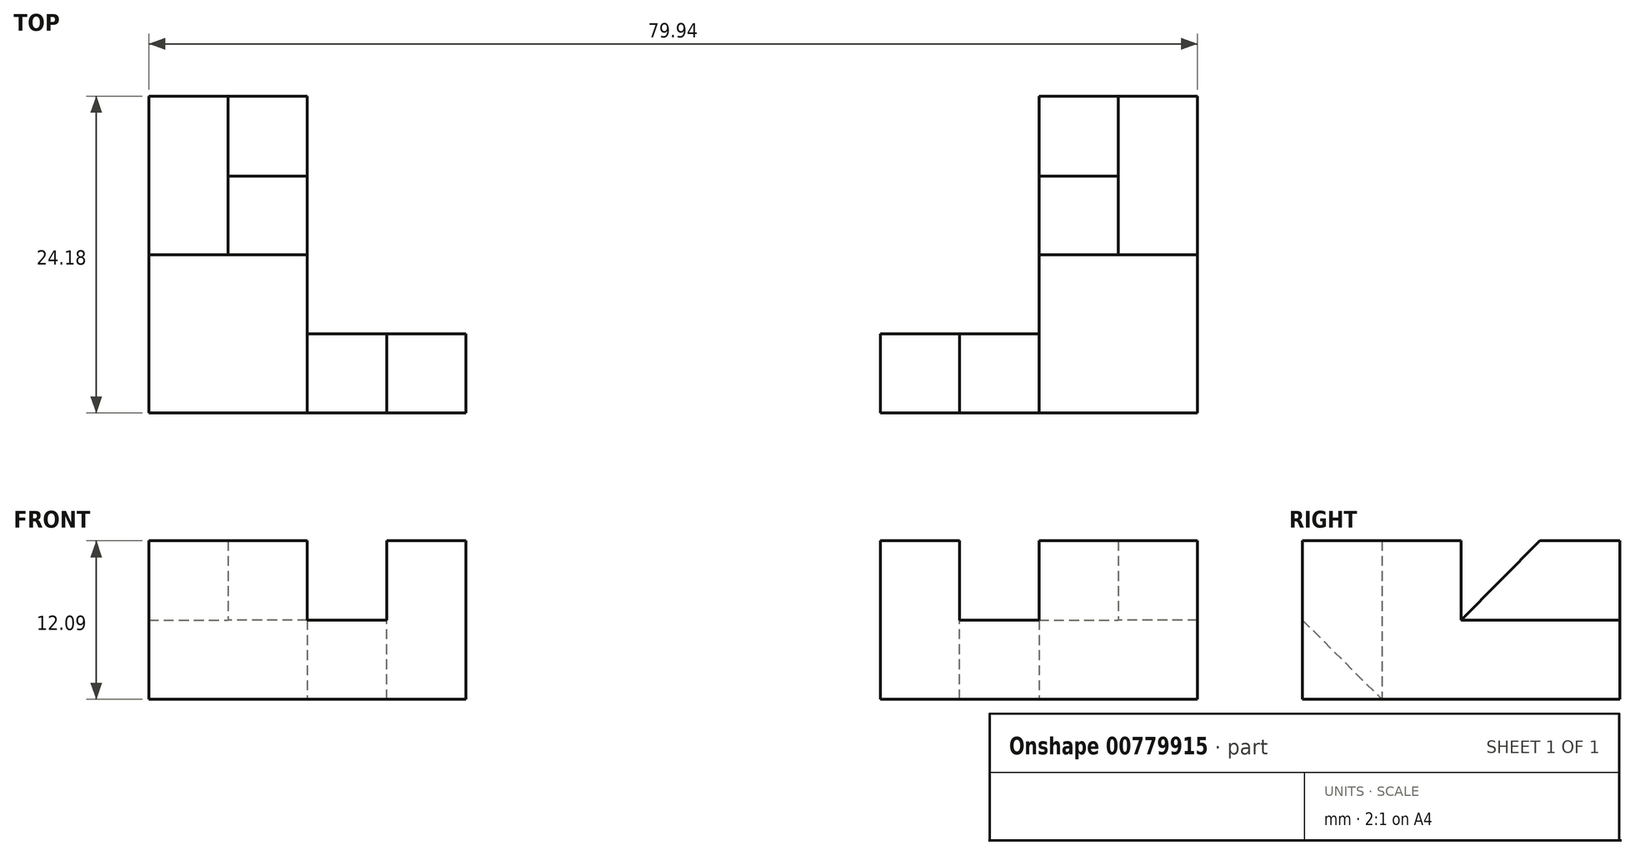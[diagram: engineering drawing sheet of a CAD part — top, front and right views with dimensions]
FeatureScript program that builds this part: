
annotation { "Feature Type Name" : "Feature", "Feature Type Description" : "" }
export const myFeature = defineFeature(function(context is Context, id is Id, definition is map)
    precondition{}
    {
        {
            var Q0;
            Q0=qCreatedBy(makeId("Top.planeOp"),FACE);
            var sketch = newSketch(context, id + "F0", { "sketchPlane" : qUnion([Q0])});
            skLineSegment(sketch, "E0", {"start": v(-15.79, 0) * mm, "end": v(-39.97, 0) * mm});
            skLineSegment(sketch, "E1.bottom", {"start": v(-39.97, 0) * mm, "end": v(-27.88, 0) * mm});
            skLineSegment(sketch, "E1.top", {"start": v(-39.97, 12.1) * mm, "end": v(-27.88, 12.1) * mm});
            skLineSegment(sketch, "E1.left", {"start": v(-39.97, 0) * mm, "end": v(-39.97, 12.1) * mm});
            skLineSegment(sketch, "E1.right", {"start": v(-27.88, 0) * mm, "end": v(-27.88, 12.1) * mm});
            skLineSegment(sketch, "E2", {"start": v(-39.97, 24.18) * mm, "end": v(-33.92, 24.18) * mm});
            skLineSegment(sketch, "E3.bottom", {"start": v(-33.92, 24.18) * mm, "end": v(-27.88, 24.18) * mm});
            skLineSegment(sketch, "E3.top", {"start": v(-33.92, 18.14) * mm, "end": v(-27.88, 18.14) * mm});
            skLineSegment(sketch, "E3.left", {"start": v(-33.92, 24.18) * mm, "end": v(-33.92, 18.14) * mm});
            skLineSegment(sketch, "E3.right", {"start": v(-27.88, 24.18) * mm, "end": v(-27.88, 18.14) * mm});
            skLineSegment(sketch, "E4.top", {"start": v(-33.92, 12.1) * mm, "end": v(-27.88, 12.1) * mm});
            skLineSegment(sketch, "E4.left", {"start": v(-33.92, 18.14) * mm, "end": v(-33.92, 12.1) * mm});
            skLineSegment(sketch, "E4.right", {"start": v(-27.88, 18.14) * mm, "end": v(-27.88, 12.1) * mm});
            skLineSegment(sketch, "E5.bottom", {"start": v(-15.79, 0) * mm, "end": v(-21.83, 0) * mm});
            skLineSegment(sketch, "E5.top", {"start": v(-15.79, 6.05) * mm, "end": v(-21.83, 6.05) * mm});
            skLineSegment(sketch, "E5.left", {"start": v(-15.79, 0) * mm, "end": v(-15.79, 6.05) * mm});
            skLineSegment(sketch, "E5.right", {"start": v(-21.83, 0) * mm, "end": v(-21.83, 6.05) * mm});
            skLineSegment(sketch, "E6.bottom", {"start": v(-21.83, 6.05) * mm, "end": v(-27.88, 6.05) * mm});
            skLineSegment(sketch, "E6.top", {"start": v(-21.83, 0) * mm, "end": v(-27.88, 0) * mm});
            skLineSegment(sketch, "E6.left", {"start": v(-21.83, 6.05) * mm, "end": v(-21.83, 0) * mm});
            skLineSegment(sketch, "E6.right", {"start": v(-27.88, 6.05) * mm, "end": v(-27.88, 0) * mm});
            skLineSegment(sketch, "E7", {"start": v(-39.97, 24.18) * mm, "end": v(-39.97, 12.1) * mm});
            skSolve(sketch);
        }
        {
            var Q0;
            {var subQ4=sQuery(id+"F0.wireOp",EDGE,"E1.left");Q0=makeQuery(id+"F0.imprint","IMPRINT",FACE,{"disambiguationData":[TD([[makeQuery(id+"F0.imprint","IMPRINT",EDGE,{"derivedFrom":subQ4}),-1.0]])]});}
            extrude(context, id + "F1", {"entities" : qUnion([Q0]), "depth" : 12.1 * mm, "offsetDistance" : 25.4 * mm});
        }
        {
            var Q0;
            Q0=makeQuery(id+"F0.imprint","IMPRINT",FACE,{"disambiguationData":[TD([[makeQuery(id+"F0.imprint","IMPRINT",EDGE,{"derivedFrom":sQuery(id+"F0.wireOp",EDGE,"E2")}),-1.0]])]});
            extrude(context, id + "F2", {"entities" : qUnion([Q0]), "operationType" : NewBodyOperationType.ADD, "depth" : 6.05 * mm, "offsetDistance" : 25.4 * mm});
        }
        {
            var Q0;
            Q0=makeQuery(id+"F0.imprint","IMPRINT",FACE,{"disambiguationData":[TD([[makeQuery(id+"F0.imprint","IMPRINT",EDGE,{"derivedFrom":sQuery(id+"F0.wireOp",EDGE,"E3.bottom")}),-1.0]])]});
            extrude(context, id + "F3", {"entities" : qUnion([Q0]), "operationType" : NewBodyOperationType.ADD, "depth" : 12.1 * mm, "offsetDistance" : 25.4 * mm});
        }
        {
            var Q0;
            Q0=makeQuery(id+"F0.imprint","IMPRINT",FACE,{"disambiguationData":[TD([[makeQuery(id+"F0.imprint","IMPRINT",EDGE,{"derivedFrom":sQuery(id+"F0.wireOp",EDGE,"E5.top")}),1.0]])]});
            extrude(context, id + "F4", {"entities" : qUnion([Q0]), "operationType" : NewBodyOperationType.ADD, "depth" : 12.1 * mm, "offsetDistance" : 25.4 * mm});
        }
        {
            var Q0;
            {var subQ3=sQuery(id+"F0.wireOp",EDGE,"E5.right");Q0=makeQuery(id+"F0.imprint","IMPRINT",FACE,{"disambiguationData":[TD([[makeQuery(id+"F0.imprint","IMPRINT",EDGE,{"derivedFrom":subQ3}),1.0]])]});}
            extrude(context, id + "F5", {"entities" : qUnion([Q0]), "operationType" : NewBodyOperationType.ADD, "depth" : 6.05 * mm, "offsetDistance" : 25.4 * mm});
        }
        {
            var Q0;
            Q0=makeQuery(id+"F5.opExtrude","CAP_EDGE",EDGE,{"disambiguationData":[OSD([sQuery(id+"F0.wireOp",EDGE,"E6.bottom")])],"isStart":false});
            chamfer(context, id + "F6", {"entities" : qUnion([Q0]), "width" : 6.05 * mm, "tangentPropagation" : true});
        }
        {
            var Q0;
            Q0=makeQuery(id+"F0.imprint","IMPRINT",FACE,{"disambiguationData":[TD([[makeQuery(id+"F0.imprint","IMPRINT",EDGE,{"derivedFrom":sQuery(id+"F0.wireOp",EDGE,"E5.top")}),1.0]])]});
            extrude(context, id + "F7", {"entities" : qUnion([Q0]), "operationType" : NewBodyOperationType.ADD, "depth" : 12.1 * mm, "offsetDistance" : 25.4 * mm});
        }
        {
            var Q0;
            Q0=makeQuery(id+"F0.imprint","IMPRINT",FACE,{"disambiguationData":[TD([[makeQuery(id+"F0.imprint","IMPRINT",EDGE,{"derivedFrom":sQuery(id+"F0.wireOp",EDGE,"E3.top")}),-1.0]])]});
            extrude(context, id + "F8", {"entities" : qUnion([Q0]), "operationType" : NewBodyOperationType.ADD, "depth" : 12.1 * mm, "offsetDistance" : 25.4 * mm});
        }
        {
            var Q0;
            Q0=makeQuery(id+"F3.boolean.opBoolean","MERGE",FACE,{"derivedFrom":[makeQuery(id+"F2.opExtrude","SWEPT_FACE",FACE,{"disambiguationData":[OSD([sQuery(id+"F0.wireOp",EDGE,"E2")])]}),makeQuery(id+"F3.opExtrude","SWEPT_FACE",FACE,{"disambiguationData":[OSD([sQuery(id+"F0.wireOp",EDGE,"E3.bottom")])]})]});
            var sketch = newSketch(context, id + "F9", { "sketchPlane" : qUnion([Q0])});
            skSolve(sketch);
        }
        {
            var Q0;
            Q0=makeQuery(id+"F8.boolean.opBoolean","MERGE",FACE,{"derivedFrom":[makeQuery(id+"F3.opExtrude","SWEPT_FACE",FACE,{"disambiguationData":[OSD([sQuery(id+"F0.wireOp",EDGE,"E3.left")])]}),makeQuery(id+"F8.opExtrude","SWEPT_FACE",FACE,{"disambiguationData":[OSD([sQuery(id+"F0.wireOp",EDGE,"E4.left")])]})]});
            var sketch = newSketch(context, id + "F10", { "sketchPlane" : qUnion([Q0])});
            skLineSegment(sketch, "E8", {"start": v(-24.18, 12.1) * mm, "end": v(-18.08, 12.1) * mm});
            skLineSegment(sketch, "E9", {"start": v(-18.08, 12.1) * mm, "end": v(-12.1, 6.05) * mm});
            skSolve(sketch);
        }
        {
            var Q0;
            {var subQ0=sQuery(id+"F10.wireOp",EDGE,"E9");Q0=makeQuery(id+"F10.imprint","IMPRINT",FACE,{"disambiguationData":[TD([[makeQuery(id+"F10.imprint","IMPRINT",EDGE,{"derivedFrom":subQ0}),1.0]])]});}
            var Q1;
            Q1=makeQuery(id+"F8.boolean.opBoolean","MERGE",FACE,{"derivedFrom":[makeQuery(id+"F3.opExtrude","SWEPT_FACE",FACE,{"disambiguationData":[OSD([sQuery(id+"F0.wireOp",EDGE,"E3.right")])]}),makeQuery(id+"F1.opExtrude","SWEPT_FACE",FACE,{"disambiguationData":[OSD([sQuery(id+"F0.wireOp",EDGE,"E1.right")])]}),makeQuery(id+"F8.opExtrude","SWEPT_FACE",FACE,{"disambiguationData":[OSD([sQuery(id+"F0.wireOp",EDGE,"E4.right")])]})]});
            extrude(context, id + "F11", {"entities" : qUnion([Q0]), "operationType" : NewBodyOperationType.REMOVE, "endBound" : BoundingType.UP_TO_SURFACE, "oppositeDirection" : true, "depth" : 2.97 * mm, "endBoundEntityFace" : qUnion([Q1]), "offsetDistance" : 25.4 * mm});
        }
        {
            var Q0;
            Q0=makeQuery(id+"F1.opExtrude","SWEPT_BODY",BODY,{"disambiguationData":[OSD([sQuery(id+"F0.wireOp",EDGE,"E0"),sQuery(id+"F0.wireOp",EDGE,"E1.top"),sQuery(id+"F0.wireOp",EDGE,"E1.left"),sQuery(id+"F0.wireOp",EDGE,"E1.right")])]});
            var Q1;
            Q1=qCreatedBy(makeId("Right.planeOp"),FACE);
            mirror(context, id + "F12", {"entities" : qUnion([Q0]), "mirrorPlane" : qUnion([Q1])});
        }
    });
